# Revit family: Vitodens 100-W B1HE 85
name_source: partatom
category: Mechanical Equipment
units: mm (PartAtom-declared; Revit-internal decimal feet)

## family parameters
Always vertical = Yes
Classification = None
Cut with Voids When Loaded = No
OmniClass Number = 23.75.10.11.14.14
OmniClass Title = Condensing Boilers
Part Type = Normal
Room Calculation Point = No
Round Connector Dimension = Use Diameter
Shared = No
Work Plane-Based = No

## types (1)
- Standard
    Connector_10_Diameter = 76 mm
    Connector_2_Diameter = 19 mm
    Connector_3_Diameter = 19 mm
    Connector_4_Diameter = 19 mm
    Connector_5_Diameter = 19 mm
    Connector_6_Diameter = 19 mm
    Connector_7_Diameter = 76 mm
    Connector_8_Diameter = 127 mm
    Connector_9_Diameter = 76 mm
    Default Elevation = 0 mm  [stored 0 ft]
    Description = Wall Hung Condensing Boiler
    Manufacturer = Viessmann
    Model = Vitodens 100-W B1HE-85
    URL = www.viessmann.com

note: [stored X ft] marks values corroborated as IEEE doubles in the binary element streams (Revit-internal decimal feet)

## geometry (parser evidence)
native form markers: Sweep x2
no freeform markers — native parametric forms only
